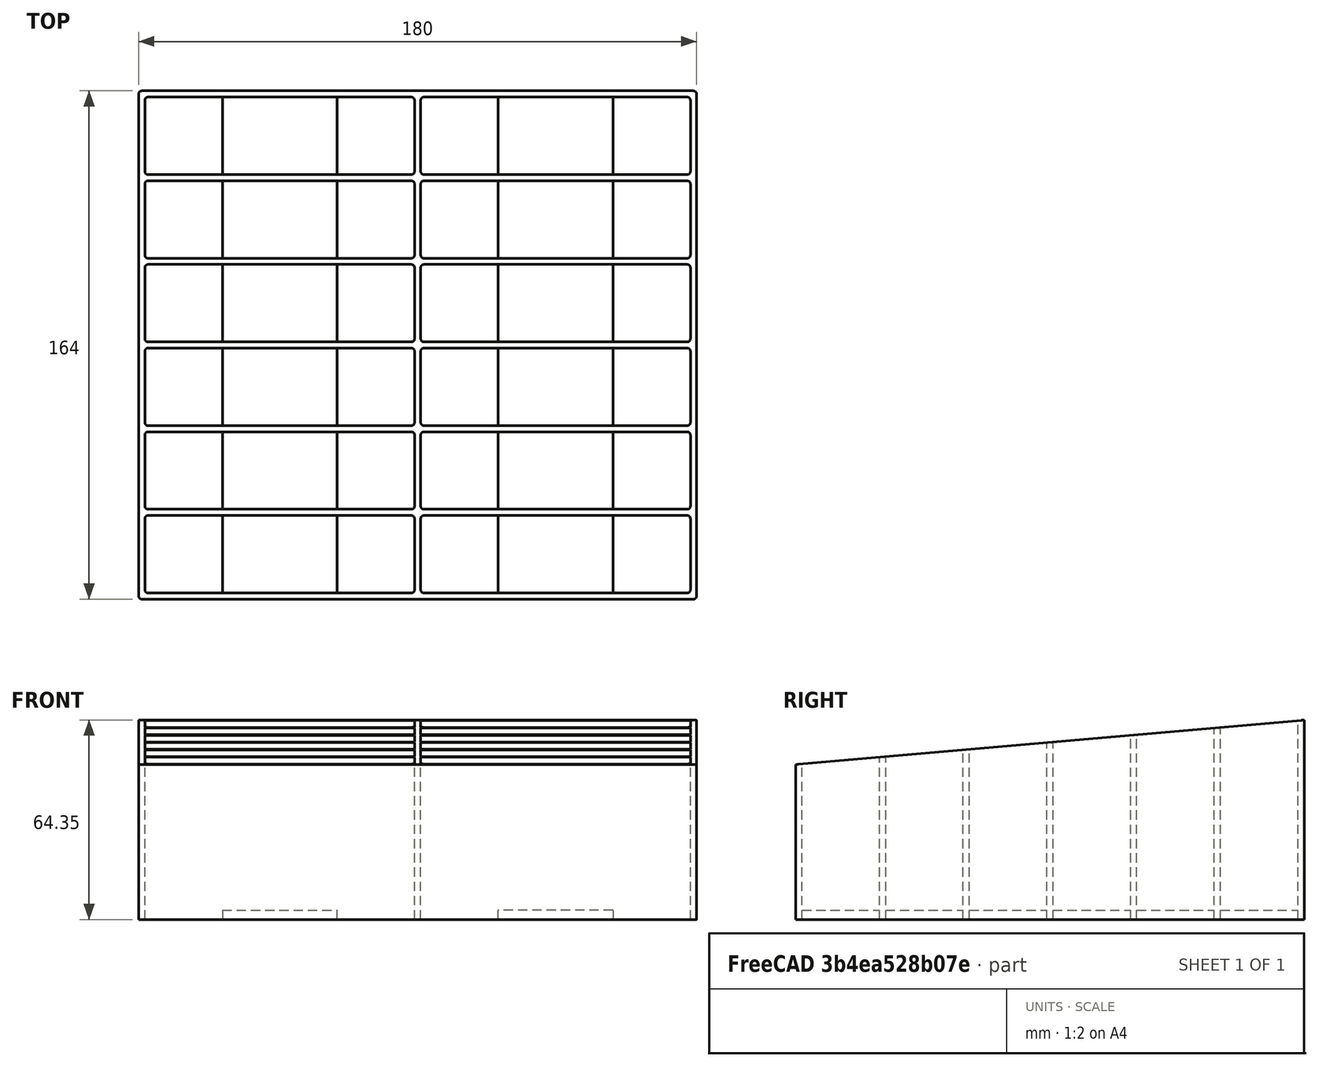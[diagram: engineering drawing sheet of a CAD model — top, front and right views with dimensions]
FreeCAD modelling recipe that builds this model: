
FCSTD DOCUMENT  (FreeCAD 0.20R)
Label: porte portable
License: All rights reserved
LicenseURL: http://en.wikipedia.org/wiki/All_rights_reserved
objects: Sketcher::SketchObject×3, PartDesign::Pad×2, PartDesign::Pocket×1, PartDesign::Body×1
note: 10 computed .brp shape members not serialized (recipe doc carries the construction recipe); baked Part::Feature solids carry a one-line shape summary decoded from their .brp

FEATURE [Sketcher::SketchObject] Sketch
  FullyConstrained = false
  sketch-geometry (104):
    g0: ArcOfCircle CenterX=3 CenterY=26 CenterZ=0 NormalX=0 NormalY=0 NormalZ=1 AngleXU=0 Radius=1 StartAngle=1.5708 EndAngle=3.14159
    g1: LineSegment StartX=2 StartY=3 StartZ=0 EndX=2 EndY=26 EndZ=0
    g2: ArcOfCircle CenterX=3 CenterY=3 CenterZ=0 NormalX=0 NormalY=0 NormalZ=1 AngleXU=0 Radius=1 StartAngle=3.14159 EndAngle=4.71239
    g3: LineSegment StartX=3 StartY=2 StartZ=0 EndX=88 EndY=2 EndZ=0
    g4: ArcOfCircle CenterX=88 CenterY=3 CenterZ=0 NormalX=0 NormalY=0 NormalZ=1 AngleXU=0 Radius=1 StartAngle=4.71239 EndAngle=6.28319
    g5: LineSegment StartX=89 StartY=3 StartZ=0 EndX=89 EndY=26 EndZ=0
    g6: LineSegment StartX=3 StartY=27 StartZ=0 EndX=88 EndY=27 EndZ=0
    g7: ArcOfCircle CenterX=88 CenterY=26 CenterZ=0 NormalX=0 NormalY=0 NormalZ=1 AngleXU=0 Radius=1 StartAngle=0 EndAngle=1.5708
    g8: ArcOfCircle CenterX=3 CenterY=30 CenterZ=0 NormalX=0 NormalY=0 NormalZ=1 AngleXU=0 Radius=1 StartAngle=3.14159 EndAngle=4.71239
    g9: LineSegment StartX=2 StartY=53 StartZ=0 EndX=2 EndY=30 EndZ=0
    g10: ArcOfCircle CenterX=3 CenterY=53 CenterZ=0 NormalX=0 NormalY=0 NormalZ=1 AngleXU=0 Radius=1 StartAngle=1.5708 EndAngle=3.14159
    g11: LineSegment StartX=3 StartY=54 StartZ=0 EndX=88 EndY=54 EndZ=0
    g12: ArcOfCircle CenterX=88 CenterY=53 CenterZ=0 NormalX=0 NormalY=0 NormalZ=1 AngleXU=0 Radius=1 StartAngle=0 EndAngle=1.5708
    g13: LineSegment StartX=89 StartY=53 StartZ=0 EndX=89 EndY=30 EndZ=0
    g14: LineSegment StartX=3 StartY=29 StartZ=0 EndX=88 EndY=29 EndZ=0
    g15: ArcOfCircle CenterX=88 CenterY=30 CenterZ=0 NormalX=0 NormalY=0 NormalZ=1 AngleXU=0 Radius=1 StartAngle=4.71239 EndAngle=6.28319
    g16: ArcOfCircle CenterX=3 CenterY=84 CenterZ=0 NormalX=0 NormalY=0 NormalZ=1 AngleXU=0 Radius=1 StartAngle=3.14159 EndAngle=4.71239
    g17: LineSegment StartX=2 StartY=107 StartZ=0 EndX=2 EndY=84 EndZ=0
    g18: ArcOfCircle CenterX=3 CenterY=107 CenterZ=0 NormalX=0 NormalY=0 NormalZ=1 AngleXU=0 Radius=1 StartAngle=1.5708 EndAngle=3.14159
    g19: LineSegment StartX=3 StartY=108 StartZ=0 EndX=88 EndY=108 EndZ=0
    g20: ArcOfCircle CenterX=88 CenterY=107 CenterZ=0 NormalX=0 NormalY=0 NormalZ=1 AngleXU=0 Radius=1 StartAngle=0 EndAngle=1.5708
    g21: LineSegment StartX=89 StartY=107 StartZ=0 EndX=89 EndY=84 EndZ=0
    g22: LineSegment StartX=3 StartY=83 StartZ=0 EndX=88 EndY=83 EndZ=0
    g23: ArcOfCircle CenterX=88 CenterY=84 CenterZ=0 NormalX=0 NormalY=0 NormalZ=1 AngleXU=0 Radius=1 StartAngle=4.71239 EndAngle=6.28319
    g24: ArcOfCircle CenterX=3 CenterY=80 CenterZ=0 NormalX=0 NormalY=0 NormalZ=1 AngleXU=0 Radius=1 StartAngle=1.5708 EndAngle=3.14159
    g25: LineSegment StartX=2 StartY=57 StartZ=0 EndX=2 EndY=80 EndZ=0
    g26: ArcOfCircle CenterX=3 CenterY=57 CenterZ=0 NormalX=0 NormalY=0 NormalZ=1 AngleXU=0 Radius=1 StartAngle=3.14159 EndAngle=4.71239
    g27: LineSegment StartX=3 StartY=56 StartZ=0 EndX=88 EndY=56 EndZ=0
    g28: ArcOfCircle CenterX=88 CenterY=57 CenterZ=0 NormalX=0 NormalY=0 NormalZ=1 AngleXU=0 Radius=1 StartAngle=4.71239 EndAngle=6.28319
    g29: LineSegment StartX=89 StartY=57 StartZ=0 EndX=89 EndY=80 EndZ=0
    g30: LineSegment StartX=3 StartY=81 StartZ=0 EndX=88 EndY=81 EndZ=0
    g31: ArcOfCircle CenterX=88 CenterY=80 CenterZ=0 NormalX=0 NormalY=0 NormalZ=1 AngleXU=0 Radius=1 StartAngle=0 EndAngle=1.5708
    g32: ArcOfCircle CenterX=3 CenterY=134 CenterZ=0 NormalX=0 NormalY=0 NormalZ=1 AngleXU=0 Radius=1 StartAngle=1.5708 EndAngle=3.14159
    g33: LineSegment StartX=2 StartY=111 StartZ=0 EndX=2 EndY=134 EndZ=0
    g34: ArcOfCircle CenterX=3 CenterY=111 CenterZ=0 NormalX=0 NormalY=0 NormalZ=1 AngleXU=0 Radius=1 StartAngle=3.14159 EndAngle=4.71239
    g35: LineSegment StartX=3 StartY=110 StartZ=0 EndX=88 EndY=110 EndZ=0
    g36: ArcOfCircle CenterX=88 CenterY=111 CenterZ=0 NormalX=0 NormalY=0 NormalZ=1 AngleXU=0 Radius=1 StartAngle=4.71239 EndAngle=6.28319
    g37: LineSegment StartX=89 StartY=111 StartZ=0 EndX=89 EndY=134 EndZ=0
    g38: LineSegment StartX=3 StartY=135 StartZ=0 EndX=88 EndY=135 EndZ=0
    g39: ArcOfCircle CenterX=88 CenterY=134 CenterZ=0 NormalX=0 NormalY=0 NormalZ=1 AngleXU=0 Radius=1 StartAngle=0 EndAngle=1.5708
    g40: ArcOfCircle CenterX=3 CenterY=138 CenterZ=0 NormalX=0 NormalY=0 NormalZ=1 AngleXU=0 Radius=1 StartAngle=3.14159 EndAngle=4.71239
    g41: LineSegment StartX=2 StartY=161 StartZ=0 EndX=2 EndY=138 EndZ=0
    g42: ArcOfCircle CenterX=3 CenterY=161 CenterZ=0 NormalX=0 NormalY=0 NormalZ=1 AngleXU=0 Radius=1 StartAngle=1.5708 EndAngle=3.14159
    g43: LineSegment StartX=3 StartY=162 StartZ=0 EndX=88 EndY=162 EndZ=0
    g44: ArcOfCircle CenterX=88 CenterY=161 CenterZ=0 NormalX=0 NormalY=0 NormalZ=1 AngleXU=0 Radius=1 StartAngle=0 EndAngle=1.5708
    g45: LineSegment StartX=89 StartY=161 StartZ=0 EndX=89 EndY=138 EndZ=0
    g46: LineSegment StartX=3 StartY=137 StartZ=0 EndX=88 EndY=137 EndZ=0
    g47: ArcOfCircle CenterX=88 CenterY=138 CenterZ=0 NormalX=0 NormalY=0 NormalZ=1 AngleXU=0 Radius=1 StartAngle=4.71239 EndAngle=6.28319
    g48: ArcOfCircle CenterX=177 CenterY=26 CenterZ=0 NormalX=0 NormalY=0 NormalZ=1 AngleXU=0 Radius=1 StartAngle=0 EndAngle=1.5708
    g49: LineSegment StartX=178 StartY=3 StartZ=0 EndX=178 EndY=26 EndZ=0
    g50: ArcOfCircle CenterX=177 CenterY=3 CenterZ=0 NormalX=0 NormalY=0 NormalZ=1 AngleXU=0 Radius=1 StartAngle=4.71239 EndAngle=6.28319
    g51: LineSegment StartX=177 StartY=2 StartZ=0 EndX=92 EndY=2 EndZ=0
    g52: ArcOfCircle CenterX=92 CenterY=3 CenterZ=0 NormalX=0 NormalY=0 NormalZ=1 AngleXU=0 Radius=1 StartAngle=3.14159 EndAngle=4.71239
    g53: LineSegment StartX=91 StartY=3 StartZ=0 EndX=91 EndY=26 EndZ=0
    g54: LineSegment StartX=177 StartY=27 StartZ=0 EndX=92 EndY=27 EndZ=0
    g55: ArcOfCircle CenterX=92 CenterY=26 CenterZ=0 NormalX=0 NormalY=0 NormalZ=1 AngleXU=0 Radius=1 StartAngle=1.5708 EndAngle=3.14159
    g56: ArcOfCircle CenterX=177 CenterY=30 CenterZ=0 NormalX=0 NormalY=0 NormalZ=1 AngleXU=0 Radius=1 StartAngle=4.71239 EndAngle=6.28319
    g57: LineSegment StartX=178 StartY=53 StartZ=0 EndX=178 EndY=30 EndZ=0
    g58: ArcOfCircle CenterX=177 CenterY=53 CenterZ=0 NormalX=0 NormalY=0 NormalZ=1 AngleXU=0 Radius=1 StartAngle=0 EndAngle=1.5708
    g59: LineSegment StartX=177 StartY=54 StartZ=0 EndX=92 EndY=54 EndZ=0
    g60: ArcOfCircle CenterX=92 CenterY=53 CenterZ=0 NormalX=0 NormalY=0 NormalZ=1 AngleXU=0 Radius=1 StartAngle=1.5708 EndAngle=3.14159
    g61: LineSegment StartX=91 StartY=53 StartZ=0 EndX=91 EndY=30 EndZ=0
    g62: LineSegment StartX=177 StartY=29 StartZ=0 EndX=92 EndY=29 EndZ=0
    g63: ArcOfCircle CenterX=92 CenterY=30 CenterZ=0 NormalX=0 NormalY=0 NormalZ=1 AngleXU=0 Radius=1 StartAngle=3.14159 EndAngle=4.71239
    g64: ArcOfCircle CenterX=177 CenterY=84 CenterZ=0 NormalX=0 NormalY=0 NormalZ=1 AngleXU=0 Radius=1 StartAngle=4.71239 EndAngle=6.28319
    g65: LineSegment StartX=178 StartY=107 StartZ=0 EndX=178 EndY=84 EndZ=0
    g66: ArcOfCircle CenterX=177 CenterY=107 CenterZ=0 NormalX=0 NormalY=0 NormalZ=1 AngleXU=0 Radius=1 StartAngle=0 EndAngle=1.5708
    g67: LineSegment StartX=177 StartY=108 StartZ=0 EndX=92 EndY=108 EndZ=0
    g68: ArcOfCircle CenterX=92 CenterY=107 CenterZ=0 NormalX=0 NormalY=0 NormalZ=1 AngleXU=0 Radius=1 StartAngle=1.5708 EndAngle=3.14159
    g69: LineSegment StartX=91 StartY=107 StartZ=0 EndX=91 EndY=84 EndZ=0
    g70: LineSegment StartX=177 StartY=83 StartZ=0 EndX=92 EndY=83 EndZ=0
    g71: ArcOfCircle CenterX=92 CenterY=84 CenterZ=0 NormalX=0 NormalY=0 NormalZ=1 AngleXU=0 Radius=1 StartAngle=3.14159 EndAngle=4.71239
    g72: ArcOfCircle CenterX=177 CenterY=80 CenterZ=0 NormalX=0 NormalY=0 NormalZ=1 AngleXU=0 Radius=1 StartAngle=0 EndAngle=1.5708
    g73: LineSegment StartX=178 StartY=57 StartZ=0 EndX=178 EndY=80 EndZ=0
    g74: ArcOfCircle CenterX=177 CenterY=57 CenterZ=0 NormalX=0 NormalY=0 NormalZ=1 AngleXU=0 Radius=1 StartAngle=4.71239 EndAngle=6.28319
    g75: LineSegment StartX=177 StartY=56 StartZ=0 EndX=92 EndY=56 EndZ=0
    g76: ArcOfCircle CenterX=92 CenterY=57 CenterZ=0 NormalX=0 NormalY=0 NormalZ=1 AngleXU=0 Radius=1 StartAngle=3.14159 EndAngle=4.71239
    g77: LineSegment StartX=91 StartY=57 StartZ=0 EndX=91 EndY=80 EndZ=0
    g78: LineSegment StartX=177 StartY=81 StartZ=0 EndX=92 EndY=81 EndZ=0
    g79: ArcOfCircle CenterX=92 CenterY=80 CenterZ=0 NormalX=0 NormalY=0 NormalZ=1 AngleXU=0 Radius=1 StartAngle=1.5708 EndAngle=3.14159
    g80: ArcOfCircle CenterX=177 CenterY=134 CenterZ=0 NormalX=0 NormalY=0 NormalZ=1 AngleXU=0 Radius=1 StartAngle=0 EndAngle=1.5708
    g81: LineSegment StartX=178 StartY=111 StartZ=0 EndX=178 EndY=134 EndZ=0
    g82: ArcOfCircle CenterX=177 CenterY=111 CenterZ=0 NormalX=0 NormalY=0 NormalZ=1 AngleXU=0 Radius=1 StartAngle=4.71239 EndAngle=6.28319
    g83: LineSegment StartX=177 StartY=110 StartZ=0 EndX=92 EndY=110 EndZ=0
    g84: ArcOfCircle CenterX=92 CenterY=111 CenterZ=0 NormalX=0 NormalY=0 NormalZ=1 AngleXU=0 Radius=1 StartAngle=3.14159 EndAngle=4.71239
    g85: LineSegment StartX=91 StartY=111 StartZ=0 EndX=91 EndY=134 EndZ=0
    g86: LineSegment StartX=177 StartY=135 StartZ=0 EndX=92 EndY=135 EndZ=0
    g87: ArcOfCircle CenterX=92 CenterY=134 CenterZ=0 NormalX=0 NormalY=0 NormalZ=1 AngleXU=0 Radius=1 StartAngle=1.5708 EndAngle=3.14159
    g88: ArcOfCircle CenterX=177 CenterY=138 CenterZ=0 NormalX=0 NormalY=0 NormalZ=1 AngleXU=0 Radius=1 StartAngle=4.71239 EndAngle=6.28319
    g89: LineSegment StartX=178 StartY=161 StartZ=0 EndX=178 EndY=138 EndZ=0
    g90: ArcOfCircle CenterX=177 CenterY=161 CenterZ=0 NormalX=0 NormalY=0 NormalZ=1 AngleXU=0 Radius=1 StartAngle=0 EndAngle=1.5708
    g91: LineSegment StartX=177 StartY=162 StartZ=0 EndX=92 EndY=162 EndZ=0
    g92: ArcOfCircle CenterX=92 CenterY=161 CenterZ=0 NormalX=0 NormalY=0 NormalZ=1 AngleXU=0 Radius=1 StartAngle=1.5708 EndAngle=3.14159
    g93: LineSegment StartX=91 StartY=161 StartZ=0 EndX=91 EndY=138 EndZ=0
    g94: LineSegment StartX=177 StartY=137 StartZ=0 EndX=92 EndY=137 EndZ=0
    g95: ArcOfCircle CenterX=92 CenterY=138 CenterZ=0 NormalX=0 NormalY=0 NormalZ=1 AngleXU=0 Radius=1 StartAngle=3.14159 EndAngle=4.71239
    g96: ArcOfCircle CenterX=1 CenterY=163 CenterZ=0 NormalX=0 NormalY=0 NormalZ=1 AngleXU=0 Radius=1 StartAngle=1.5708 EndAngle=3.14159
    g97: ArcOfCircle CenterX=179 CenterY=1 CenterZ=0 NormalX=0 NormalY=0 NormalZ=1 AngleXU=0 Radius=1 StartAngle=4.71239 EndAngle=6.28319
    g98: LineSegment StartX=179 StartY=164 StartZ=0 EndX=1 EndY=164 EndZ=0
    g99: LineSegment StartX=180 StartY=1 StartZ=0 EndX=180 EndY=163 EndZ=0
    g100: ArcOfCircle CenterX=179 CenterY=163 CenterZ=0 NormalX=0 NormalY=0 NormalZ=1 AngleXU=0 Radius=1 StartAngle=0 EndAngle=1.5708
    g101: LineSegment StartX=179 StartY=0 StartZ=0 EndX=1 EndY=0 EndZ=0
    g102: LineSegment StartX=-8.5e-15 StartY=1 StartZ=0 EndX=4e-15 EndY=163 EndZ=0
    g103: ArcOfCircle CenterX=1 CenterY=1 CenterZ=0 NormalX=0 NormalY=0 NormalZ=1 AngleXU=0 Radius=1 StartAngle=3.14159 EndAngle=4.71239
FEATURE [PartDesign::Pad] Pad
  Direction = (0,0,1)
  Length = 65
  Length2 = 10
  Profile = -> Sketch
  ReferenceAxis = -> Sketch [N_Axis]
  Type = 0
FEATURE [Sketcher::SketchObject] Sketch001
  FullyConstrained = false
  MapMode = 5
  Placement = pos=(180,0,0) rot=(0.57735,0.57735,0.57735;2.0944rad)
  Support = -> [Pad]
  sketch-geometry (4):
    g0: LineSegment StartX=0 StartY=50 StartZ=0 EndX=202.777 EndY=67.7407 EndZ=0
    g1: LineSegment StartX=202.777 StartY=67.7407 StartZ=0 EndX=191.337 EndY=87.1558 EndZ=0
    g2: LineSegment StartX=191.337 StartY=87.1558 StartZ=0 EndX=-16.3523 EndY=87.1558 EndZ=0
    g3: LineSegment StartX=-16.3523 StartY=87.1558 StartZ=0 EndX=0 EndY=50 EndZ=0
  constraints (8):
    c: Coincident(g1,g0)
    c: Coincident(g2,g1)
    c: Horizontal(g2)
    c: Coincident(g3,g2)
    c: Coincident(g3,g0)
    c: PointOnObject(g0,g-2)
    c: Angle(g-1,g0) = 0.0872665
    c: DistanceY(g-1,g0) = 50
FEATURE [PartDesign::Pocket] Pocket
  BaseFeature = -> Pad
  Direction = (-1,0,0)
  Length = 5
  Length2 = 5
  Profile = -> Sketch001
  ReferenceAxis = -> Sketch001 [N_Axis]
  Type = 1
FEATURE [Sketcher::SketchObject] Sketch002
  ExternalGeometry = -> [Pocket]
  FullyConstrained = true
  MapMode = 5
  Placement = pos=(0,0,0) rot=(1,0,0;3.14159rad)
  Support = -> [Pocket]
  sketch-geometry (8):
    g0: LineSegment StartX=27 StartY=0 StartZ=0 EndX=64 EndY=0 EndZ=0
    g1: LineSegment StartX=64 StartY=0 StartZ=0 EndX=64 EndY=-164 EndZ=0
    g2: LineSegment StartX=64 StartY=-164 StartZ=0 EndX=27 EndY=-164 EndZ=0
    g3: LineSegment StartX=27 StartY=-164 StartZ=0 EndX=27 EndY=0 EndZ=0
    g4: LineSegment StartX=116 StartY=0 StartZ=0 EndX=153 EndY=0 EndZ=0
    g5: LineSegment StartX=153 StartY=0 StartZ=0 EndX=153 EndY=-164 EndZ=0
    g6: LineSegment StartX=153 StartY=-164 StartZ=0 EndX=116 EndY=-164 EndZ=0
    g7: LineSegment StartX=116 StartY=-164 StartZ=0 EndX=116 EndY=0 EndZ=0
  constraints (24):
    c: Coincident(g0,g1)
    c: Coincident(g1,g2)
    c: Coincident(g2,g3)
    c: Coincident(g3,g0)
    c: Horizontal(g0)
    c: Horizontal(g2)
    c: Vertical(g1)
    c: Vertical(g3)
    c: PointOnObject(g0,g-1)
    c: PointOnObject(g1,g-3)
    c: DistanceX(g-5,g0) = 25
    c: DistanceX(g0,g-4) = 25
    c: Coincident(g4,g5)
    c: Coincident(g5,g6)
    c: Coincident(g6,g7)
    c: Coincident(g7,g4)
    c: Horizontal(g4)
    c: Horizontal(g6)
    c: Vertical(g5)
    c: Vertical(g7)
    c: PointOnObject(g4,g-1)
    c: PointOnObject(g5,g-3)
    c: DistanceX(g-6,g6) = 25
    c: DistanceX(g4,g-7) = 25
FEATURE [PartDesign::Pad] Pad001
  BaseFeature = -> Pocket
  Direction = (0,0,-1)
  Length = 3
  Length2 = 10
  Profile = -> Sketch002
  ReferenceAxis = -> Sketch002 [N_Axis]
  Reversed = true
  Type = 0
FEATURE [PartDesign::Body] Body
  Group = -> [Sketch,Pad,Sketch001,Pocket,Sketch002,Pad001]
  Origin = -> Origin
  Tip = -> Pad001
